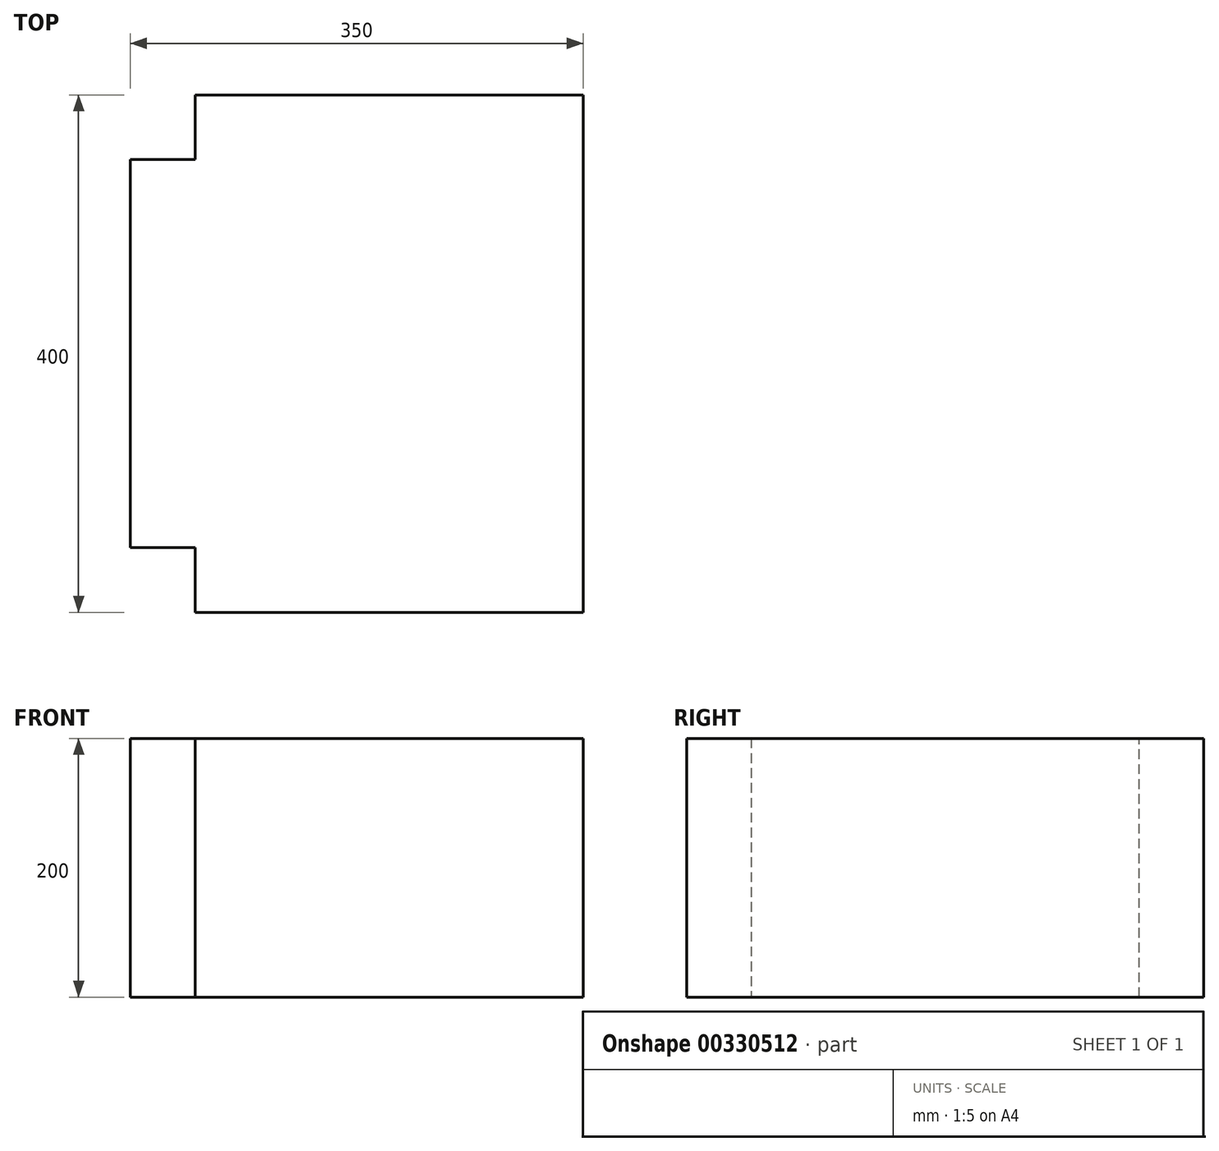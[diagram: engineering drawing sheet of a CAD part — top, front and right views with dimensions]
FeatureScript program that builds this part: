
annotation { "Feature Type Name" : "Feature", "Feature Type Description" : "" }
export const myFeature = defineFeature(function(context is Context, id is Id, definition is map)
    precondition{}
    {
        {
            var Q0;
            Q0=qCreatedBy(makeId("Top.planeOp"),FACE);
            var sketch = newSketch(context, id + "F0", { "sketchPlane" : qUnion([Q0])});
            skLineSegment(sketch, "E0.bottom", {"start": v(-143.98, 143.45) * mm, "end": v(156.02, 143.45) * mm});
            skLineSegment(sketch, "E0.top", {"start": v(-143.98, -156.55) * mm, "end": v(156.02, -156.55) * mm});
            skLineSegment(sketch, "E0.left", {"start": v(-143.98, 143.45) * mm, "end": v(-143.98, -156.55) * mm});
            skLineSegment(sketch, "E0.right", {"start": v(156.02, 143.45) * mm, "end": v(156.02, -156.55) * mm});
            skSolve(sketch);
        }
        {
            var Q0;
            Q0=makeQuery(id+"F0.imprint","IMPRINT",FACE,{"disambiguationData":[TD([[makeQuery(id+"F0.imprint","IMPRINT",EDGE,{"derivedFrom":sQuery(id+"F0.wireOp",EDGE,"E0.bottom")}),-1.0]])]});
            extrude(context, id + "F1", {"entities" : qUnion([Q0]), "depth" : 200 * mm});
        }
        {
            var Q0;
            Q0=makeQuery(id+"F1.opExtrude","SWEPT_FACE",FACE,{"disambiguationData":[OSD([sQuery(id+"F0.wireOp",EDGE,"E0.right")])]});
            var sketch = newSketch(context, id + "F2", { "sketchPlane" : qUnion([Q0])});
            skSolve(sketch);
        }
        {
            var Q0;
            {var subQ0=sQuery(id+"F0.wireOp",EDGE,"E0.right");Q0=makeQuery(id+"F2.imprint","IMPRINT",FACE,{"disambiguationData":[TD([[makeQuery(id+"F2.imprint","IMPRINT",EDGE,{"derivedFrom":makeQuery(id+"F1.opExtrude","CAP_EDGE",EDGE,{"disambiguationData":[OSD([subQ0])],"isStart":true})}),-1.0]])]});}
            extrude(context, id + "F3", {"entities" : qUnion([Q0]), "operationType" : NewBodyOperationType.ADD, "depth" : 50 * mm});
        }
        {
            var Q0;
            {var subQ0=sQuery(id+"F0.wireOp",EDGE,"E0.top");Q0=makeQuery(id+"F3.boolean.opBoolean","MERGE",FACE,{"derivedFrom":[makeQuery(id+"F1.opExtrude","SWEPT_FACE",FACE,{"disambiguationData":[OSD([subQ0])]}),makeQuery(id+"F3.opExtrude","SWEPT_FACE",FACE,{"disambiguationData":[OSD([subQ0,sQuery(id+"F0.wireOp",EDGE,"E0.right")])]})]});}
            var sketch = newSketch(context, id + "F4", { "sketchPlane" : qUnion([Q0])});
            skLineSegment(sketch, "E1.bottom", {"start": v(206.02, 200) * mm, "end": v(-93.98, 200) * mm});
            skLineSegment(sketch, "E1.top", {"start": v(206.02, 0) * mm, "end": v(-93.98, 0) * mm});
            skLineSegment(sketch, "E1.left", {"start": v(206.02, 200) * mm, "end": v(206.02, 0) * mm});
            skLineSegment(sketch, "E1.right", {"start": v(-93.98, 200) * mm, "end": v(-93.98, 0) * mm});
            skSolve(sketch);
        }
        {
            var Q0;
            Q0=makeQuery(id+"F4.imprint","IMPRINT",FACE,{"disambiguationData":[TD([[makeQuery(id+"F4.imprint","IMPRINT",EDGE,{"derivedFrom":sQuery(id+"F4.wireOp",EDGE,"E1.bottom")}),-1.0]])]});
            extrude(context, id + "F5", {"entities" : qUnion([Q0]), "operationType" : NewBodyOperationType.ADD, "depth" : 50 * mm});
        }
        {
            var Q0;
            {var subQ0=sQuery(id+"F0.wireOp",EDGE,"E0.bottom");Q0=makeQuery(id+"F3.boolean.opBoolean","MERGE",FACE,{"derivedFrom":[makeQuery(id+"F1.opExtrude","SWEPT_FACE",FACE,{"disambiguationData":[OSD([subQ0])]}),makeQuery(id+"F3.opExtrude","SWEPT_FACE",FACE,{"disambiguationData":[OSD([subQ0,sQuery(id+"F0.wireOp",EDGE,"E0.right")])]})]});}
            var sketch = newSketch(context, id + "F6", { "sketchPlane" : qUnion([Q0])});
            skLineSegment(sketch, "E2.bottom", {"start": v(-206.02, 0) * mm, "end": v(93.98, 0) * mm});
            skLineSegment(sketch, "E2.top", {"start": v(-206.02, 200) * mm, "end": v(93.98, 200) * mm});
            skLineSegment(sketch, "E2.left", {"start": v(-206.02, 0) * mm, "end": v(-206.02, 200) * mm});
            skLineSegment(sketch, "E2.right", {"start": v(93.98, 0) * mm, "end": v(93.98, 200) * mm});
            skSolve(sketch);
        }
        {
            var Q0;
            Q0=makeQuery(id+"F6.imprint","IMPRINT",FACE,{"disambiguationData":[TD([[makeQuery(id+"F6.imprint","IMPRINT",EDGE,{"derivedFrom":sQuery(id+"F6.wireOp",EDGE,"E2.bottom")}),-1.0]])]});
            extrude(context, id + "F7", {"entities" : qUnion([Q0]), "operationType" : NewBodyOperationType.ADD, "depth" : 50 * mm});
        }
    });
